# Revit family: DC_Rheem_PLM_940001UV_Disinfection
name_source: partatom
category: Electrical Fixtures
revit_build: Autodesk Revit 2017 (Build: 20160225_1515(x64)
units: mm (PartAtom-declared; Revit-internal decimal feet)

## family parameters
Cut with Voids When Loaded = No
Host = Face
Maintain Annotation Orientation = No
Part Type = Normal
Room Calculation Point = No
Round Connector Dimension = Use Diameter
Shared = No

## types (1)
- DC_Rheem_PLM_940001UV_Disinfection
    CaseMaterial_ANZRS = Rheem - Plastic_ANZRS
    Default Elevation = 0 mm  [stored 0 ft]
    Depth_ANZRS = 155 mm  [stored 0.50853 ft]
    Description = Power Supply Cabinet
    DesignBy_ANZRS = GAH
    Height_ANZRS = 360 mm  [stored 1.1811 ft]
    Manufacturer = Rheem
    Model = 940001 UV Disinfection
    PipeDia_ANZRS = 15 mm  [stored 0.0492126 ft]
    URL = http://www.rheem.com.au
    Width_ANZRS = 265 mm  [stored 0.869423 ft]

note: [stored X ft] marks values corroborated as IEEE doubles in the binary element streams (Revit-internal decimal feet)

## geometry (parser evidence)
native form markers: Blend x10, Sweep x5
no freeform markers — native parametric forms only
